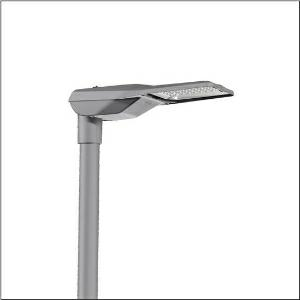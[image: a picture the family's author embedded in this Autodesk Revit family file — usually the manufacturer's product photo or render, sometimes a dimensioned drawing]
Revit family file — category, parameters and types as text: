
# Revit family: streetlight_sl_21_mini___p1_0a_5xe2a33s08hb_2caa
name_source: partatom
category: Lighting Fixtures
units: mm (PartAtom-declared; Revit-internal decimal feet)

## family parameters
Cut with Voids When Loaded = No
Host = Face
Light Source = No
Part Type = Normal
Room Calculation Point = No
Round Connector Dimension = Use Diameter
Shared = No

## types (1)
- --- (1 x LED, 9040 lm, 66 W, 3000K)
    Apparent Load = 66 VA
    CIE Flux Codes = 21 50 90 100 100
    Color Rendering = 70
    Color Temperature = 3000K
    Default Elevation = 1800 mm
    Description = Streetlight SL 21 mini, mast luminaire, primary light control with lens, of PMMA, primary optical cover: cover, of toughened safety glass, transparent, light distribution: P1.0a, light emission: direct distribution, primary light characteristic: asymmetric, installation type: side-entry, post-top, LED, High Power LED, rated luminous flux: 9.040lm, luminous efficacy: 137lm/W, light colour: 730, colour temperature: 3000K, control gear: D4i, control: overheat protection, constant luminous flux control, time-dependent luminous flux control, flexible luminous flux parameterisation, pre-setting: logarithmic dimming characteristic, mains connection: 220..240V, AC, 50/60Hz, start of lifetime: 66W, end of service life: 69W, reduction: 30W, luminaire housing, of diecast aluminium, powder-coated, SITECO metallic grey (DB 702S), corrosivity category C5 high according to DIN EN ISO 12944, please order mast flange separately, inclination adjustable: 0°, 5°, 10°, 15°, sealing non-destructively replaceable, multi-level sealing system, length: 628mm, width: 235mm, height: 110mm, mast flange for spigot size: 42mm (side-entry): 5XC10008XM4, 60/48mm (side-entry/post-top): 5XC10108XM2, 76/60mm (side-entry/post-top): 5XC10108XM1, mounting height: 4..8m, Smart Interface above, protection rating (complete): IP66, insulation class (complete): insulation class II (safety insulation), certification: CE, ENEC, ENEC+, VDE, impact resistance: IK10, permissible operating ambient temperature for outdoor applications: -40..+50°C, standard-compliant lighting for roads and squares, packaging unit: 1 piece

Light Distribution: P1.0a
    Height = 110 mm
    Lamp = 1 x LED
    Lamp Light Flux = 9040 lm
    Lamp Power = 66 W
    Lamp count = 1
    Length = 625 mm
    Luminous efficacy = 137 lm/W
    Manufacturer = Siteco
    ModVariant = No
    Model = 5XE2A33S08HB
    Number of Poles = 1
    OnlyDefault = Yes
    Power Factor = 1
    Product Name = Streetlight SL 21 mini | P1.0a
    Product group = mast luminaire | pylon top
    ProductGroupID = 6100
    Protection Class = Protection class II
    Protection Degree = IP 66
    RLX_Detail_Level = 1
    RLX_Emergency_Light_Flux = 0 lm
    RLX_Emergency_Type = 0
    RLX_Emergency_Type_DB = No
    RlxData = <blob elided: 37437 chars, md5=76e23a50>
    Socket = socket
    Standby Power = 0 W
    System Light Flux = 9040 lm
    System Power = 66 W
    Type Comments = factory setting: luminous flux: 100 % | dim-lin: 254 | 670 mA
    Type Image = l_1003515.jpg
    URL = http://relux.com
    VarID = @adj_184091
    Voltage = 0 V
    Weight = 0.00 kg
    Width = 234 mm

## geometry (parser evidence)
native form markers: Blend x4, Sweep x12
no freeform markers — native parametric forms only
